# Revit family: LOROWERK 08061.050X
name_source: partatom
category: Rohrformteile
revit_build: Autodesk Revit 2017 (Build: 20160225_1515(x64)
units: mm (PartAtom-declared; Revit-internal decimal feet)

## family parameters
Arbeitsebenenbasiert = Nein
Beim Laden mit Abzugskörper schneiden = Nein
Bemaßung runder Anschluss = Durchmesser verwenden
Gemeinsam genutzt = Nein
Immer vertikal = Ja
Teiletyp = Unterbricht

## types (1)
- LOROWERK 08061.050X
    Beschreibung = LORO-X Sicherungsschelle mit Ausklinkung DN50
    CONNECTOR0_DIAMETER_dZ_0r = 50 mm
    CONNECTOR0_dZ_00 = 60 mm
    CONNECTOR0_dZ_01 = 61 mm
    CONNECTOR0_ref_dZ = 61 mm
    CONNECTOR1_DIAMETER_dZ_0r = 50 mm
    CONNECTOR1_dZ_00 = 1 mm  [stored 0.00328084 ft]
    CONNECTOR1_ref_dZ = 1 mm  [stored 0.00328084 ft]
    DATANORM = 08061.050X
    HAN = 08061.050X
    HeinzeBIM = https://www.heinze.de
    Hersteller = LOROWERK K.H. Vahlbrauk GmbH & Co. KG
    Typname = LORO-X Sicherungsschelle mit Ausklinkung DN50
    VDIBSN = 01902900000000000000000000000000000000000000000001000000000000000000

note: [stored X ft] marks values corroborated as IEEE doubles in the binary element streams (Revit-internal decimal feet)
